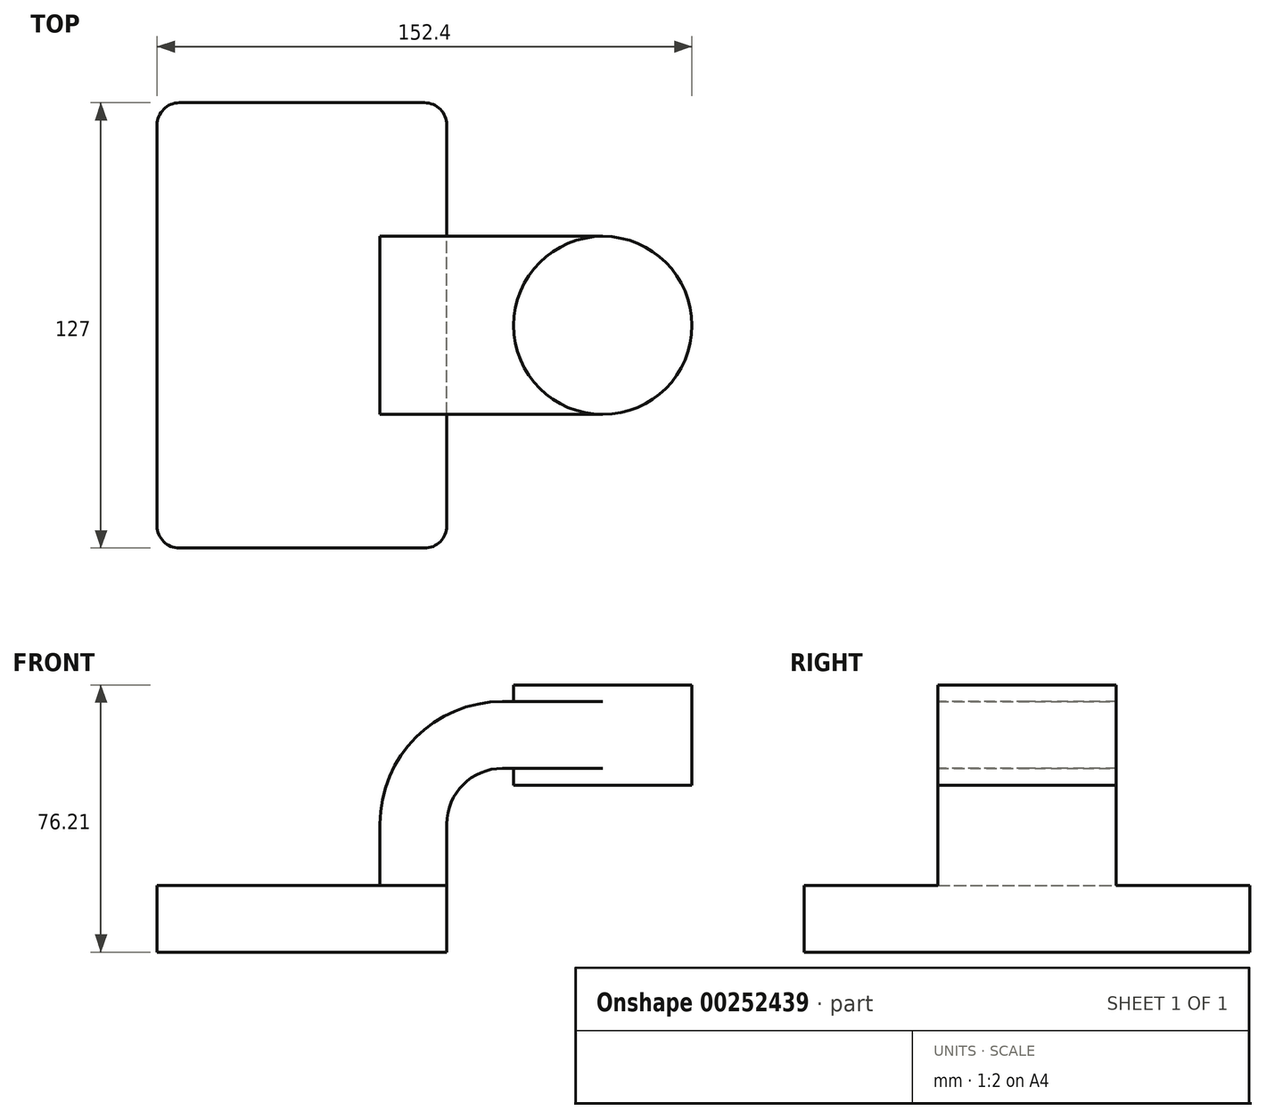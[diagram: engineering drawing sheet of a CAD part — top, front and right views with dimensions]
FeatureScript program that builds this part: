
annotation { "Feature Type Name" : "Feature", "Feature Type Description" : "" }
export const myFeature = defineFeature(function(context is Context, id is Id, definition is map)
    precondition{}
    {
        {
            var Q0;
            Q0=qCreatedBy(makeId("Front.planeOp"),FACE);
            var sketch = newSketch(context, id + "F0", { "sketchPlane" : qUnion([Q0])});
            skLineSegment(sketch, "E0.bottom", {"start": v(41.27, 9.53) * mm, "end": v(-41.28, 9.53) * mm});
            skLineSegment(sketch, "E0.top", {"start": v(41.28, -9.52) * mm, "end": v(-41.27, -9.52) * mm});
            skLineSegment(sketch, "E0.left", {"start": v(41.28, 9.53) * mm, "end": v(41.28, -9.52) * mm});
            skLineSegment(sketch, "E0.right", {"start": v(-41.28, 9.53) * mm, "end": v(-41.27, -9.52) * mm});
            skPoint(sketch, "E0.middle", {"position": v(0, 0) * mm});
            skPoint(sketch, "E1.middle", {"position": v(41.27, 9.53) * mm});
            skLineSegment(sketch, "E2.bottom", {"start": v(111.13, 66.68) * mm, "end": v(60.33, 66.68) * mm});
            skLineSegment(sketch, "E2.top", {"start": v(111.13, 38.1) * mm, "end": v(60.33, 38.1) * mm});
            skLineSegment(sketch, "E2.left", {"start": v(111.13, 66.68) * mm, "end": v(111.13, 38.1) * mm});
            skLineSegment(sketch, "E2.right", {"start": v(60.33, 66.68) * mm, "end": v(60.33, 38.1) * mm});
            skPoint(sketch, "E2.middle", {"position": v(85.73, 52.39) * mm});
            skLineSegment(sketch, "E3", {"start": v(41.27, 9.53) * mm, "end": v(41.27, 27) * mm});
            skArc(sketch, "E4", {"start": v(41.27, 27) * mm, "mid": v(45.92, 38.23) * mm, "end": v(57.15, 42.88) * mm});
            skLineSegment(sketch, "E5", {"start": v(57.15, 42.88) * mm, "end": v(85.73, 42.88) * mm});
            skLineSegment(sketch, "E6.0", {"start": v(57.15, 61.93) * mm, "end": v(85.73, 61.93) * mm});
            skArc(sketch, "E6.1", {"start": v(22.23, 27) * mm, "mid": v(32.45, 51.7) * mm, "end": v(57.15, 61.93) * mm});
            skLineSegment(sketch, "E6.2", {"start": v(22.22, 9.53) * mm, "end": v(22.22, 27) * mm});
            skLineSegment(sketch, "E7", {"start": v(85.73, 38.1) * mm, "end": v(85.73, 66.68) * mm});
            skFitSpline(sketch, "E8", {"points": [v(-41.28, 9.52) * mm, v(57.15, 61.93) * mm], "startDerivative": vector(69.68, 91.38) * mm, "endDerivative": vector(134.27, -12.6) * mm});
            skSolve(sketch);
        }
        {
            var Q0;
            Q0=makeQuery(id+"F0.imprint","IMPRINT",FACE,{"disambiguationData":[TD([[makeQuery(id+"F0.imprint","IMPRINT",EDGE,{"derivedFrom":sQuery(id+"F0.wireOp",EDGE,"E0.top")}),-1.0]])]});
            extrude(context, id + "F1", {"entities" : qUnion([Q0]), "endBound" : BoundingType.SYMMETRIC, "depth" : 127 * mm});
        }
        {
            var Q0;
            {var subQ1=sQuery(id+"F0.wireOp",EDGE,"E3");Q0=makeQuery(id+"F0.imprint","IMPRINT",FACE,{"disambiguationData":[TD([[makeQuery(id+"F0.imprint","IMPRINT",EDGE,{"derivedFrom":subQ1}),1.0]])]});}
            var Q1;
            {var subQ0=sQuery(id+"F0.wireOp",EDGE,"E6.0");var subQ1=sQuery(id+"F0.wireOp",EDGE,"E2.right");var subQ2=makeQuery(id+"F0.imprint","INTERSECT",VERTEX,{"derivedFrom":[subQ1,subQ0]});Q1=makeQuery(id+"F0.imprint","IMPRINT",FACE,{"disambiguationData":[TD([[makeQuery(id+"F0.imprint","IMPRINT",EDGE,{"disambiguationData":[TD([[subQ2,-1.0]])],"derivedFrom":subQ1}),1.0]])]});}
            extrude(context, id + "F2", {"entities" : qUnion([Q0, Q1]), "operationType" : NewBodyOperationType.ADD, "endBound" : BoundingType.SYMMETRIC, "depth" : 50.8 * mm});
        }
        {
            var Q0;
            Q0=makeQuery(id+"F0.imprint","IMPRINT",FACE,{"disambiguationData":[TD([[makeQuery(id+"F0.imprint","IMPRINT",EDGE,{"derivedFrom":sQuery(id+"F0.wireOp",EDGE,"E6.1")}),1.0]])]});
            extrude(context, id + "F3", {"entities" : qUnion([Q0]), "operationType" : NewBodyOperationType.ADD, "endBound" : BoundingType.SYMMETRIC, "depth" : 15.88 * mm});
        }
        {
            var Q0;
            {var subQ0=sQuery(id+"F0.wireOp",EDGE,"E2.left");Q0=makeQuery(id+"F0.imprint","IMPRINT",FACE,{"disambiguationData":[TD([[makeQuery(id+"F0.imprint","IMPRINT",EDGE,{"derivedFrom":subQ0}),-1.0]])]});}
            var Q1;
            Q1=sQuery(id+"F0.wireOp",EDGE,"E7");
            revolve(context, id + "F4", {"operationType" : NewBodyOperationType.ADD, "entities" : qUnion([Q0]), "axis" : qUnion([Q1]), "revolveType" : RevolveType.FULL});
        }
        {
            var Q0;
            Q0=makeQuery(id+"F1.opExtrude","CAP_EDGE",EDGE,{"disambiguationData":[OSD([sQuery(id+"F0.wireOp",EDGE,"E0.right")])],"isStart":false});
            var Q1;
            Q1=makeQuery(id+"F1.opExtrude","CAP_EDGE",EDGE,{"disambiguationData":[OSD([sQuery(id+"F0.wireOp",EDGE,"E0.right")])],"isStart":true});
            var Q2;
            Q2=makeQuery(id+"F1.opExtrude","CAP_EDGE",EDGE,{"disambiguationData":[OSD([sQuery(id+"F0.wireOp",EDGE,"E0.left")])],"isStart":true});
            var Q3;
            Q3=makeQuery(id+"F1.opExtrude","CAP_EDGE",EDGE,{"disambiguationData":[OSD([sQuery(id+"F0.wireOp",EDGE,"E0.left")])],"isStart":false});
            fillet(context, id + "F5", {"entities" : qUnion([Q0, Q1, Q2, Q3]), "radius" : 6.35 * mm, "tangentPropagation" : true, "allowEdgeOverflow" : false});
        }
    });
